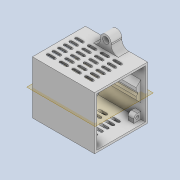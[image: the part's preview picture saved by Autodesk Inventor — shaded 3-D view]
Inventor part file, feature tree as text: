
AUTODESK INVENTOR PART (.ipt)
format: ipt  version: 2021 (Build 250183000, 183)  size: 544,256 bytes
history: native  units: mm
features: sketch x8, extrude x8, projected_geometry x5, plane x3, mirror x2, pattern_linear x1, fillet x1, hole x1
ambient origin geometry x8: Origin, YZ Plane, XZ Plane, XY Plane, X Axis, Y Axis, Z Axis, Center Point
bodies: Solid1 (feature_tree)
feature tree (29):
  sketch  "Sketch1"  dims[d0=75.0mm d1=75.0mm]
  extrude  "Extrusion1"  Depth=75.0mm
  extrude  "Extrusion2"  TaperAngle=45.0deg  [1 undecoded]
  sketch  "Sketch3"  dims[d2=3.0mm d4=45.0deg]
  plane  "Work Plane1"
  extrude  "Extrusion3"  Depth=60.5mm
  pattern_linear  "Rectangular Pattern1"  Spacing1=3.0mm  [1 undecoded]
  mirror  "Mirror1"
  extrude  "Extrusion4"  Depth=42.5mm
  plane  "Work Plane2"
  sketch  "Sketch7"  dims[d8=56.0mm]
  extrude  "Extrusion5"  [1 undecoded]
  extrude  "Extrusion6"  Depth=4.0mm
  plane  "Work Plane3"
  extrude  "Extrusion8"  Depth=5.0mm
  extrude  "Extrusion10"  Depth=8.0mm TaperAngle=0.0deg
  fillet  "Fillet3"  Radius=60.0mm
  hole  "Hole2"  [1 undecoded]
  mirror  "Mirror6"
  sketch  "Sketch5"  dims[d5=60.5mm d6=1.8mm]
  sketch  "Sketch6"  dims[d7=1.8mm]
  projected_geometry  "Projected Loop1"
  projected_geometry  "Projected Loop2"
  sketch  "Sketch8"  dims[d9=15.0mm]
  projected_geometry  "Projected Loop3"
  sketch  "Sketch12"  dims[d10=15.0mm]
  projected_geometry  "Projected Loop6"
  sketch  "Sketch13"  dims[d11=85.0mm d12=0.0mm d13=3.0mm d14=0.0mm d16=42.5mm d17=-7.853982mm d19=4.0mm d20=5.0mm d21=33.0mm d22=0.0mm d23=60.0mm d25=8.0mm d26=40.0mm d28=18.0mm d30=33.0mm d31=0.0mm d32=-6.5mm d33=4.3mm d34=5.0mm d35=5.0mm d36=7.2mm d37=8.0mm d38=0.0mm d39=4.0mm d40=0.0mm d41=5.0mm d42=5.0mm d43=7.2mm d44=4.3mm d48=3.0mm d49=3.0mm d50=3.0mm d51=4.0mm d52=0.0mm d80=15.0mm d81=12.0mm d82=15.0mm d83=0.0mm d84=10.0mm d85=9.0mm d86=6.0mm d87=15.0mm d88=9.0mm d89=90.0deg d90=8.0mm d91=20.594885mm d61=0.5mm d62=0.872665mm d63=0.5mm d64=0.872665mm]
  projected_geometry  "Projected Loop7"
note: 4 required parameter values undecoded (feature->parameter linkage not recoverable at this tier; creation-order binding heuristic only, values carry confidence <= 0.55)
